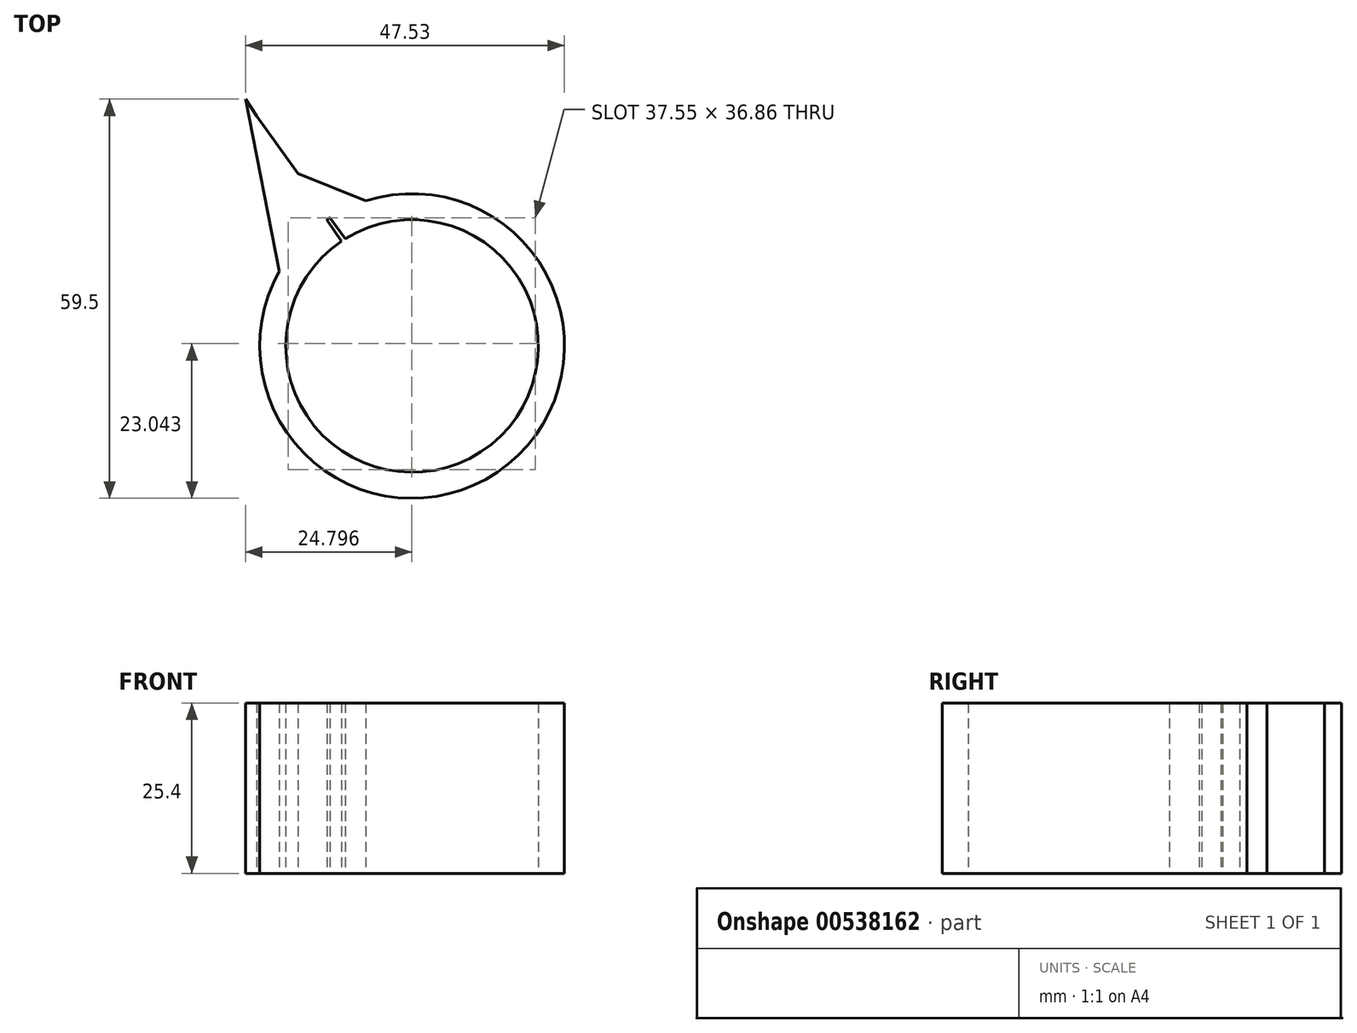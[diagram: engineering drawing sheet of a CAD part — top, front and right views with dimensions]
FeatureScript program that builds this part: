
annotation { "Feature Type Name" : "Feature", "Feature Type Description" : "" }
export const myFeature = defineFeature(function(context is Context, id is Id, definition is map)
    precondition{}
    {
        {
            var Q0;
            Q0=qCreatedBy(makeId("Top.planeOp"),FACE);
            var sketch = newSketch(context, id + "F0", { "sketchPlane" : qUnion([Q0])});
            skCircle(sketch, "E0", {"center": v(0, 0) * mm, "radius": 18.82 * mm});
            skCircle(sketch, "E1", {"center": v(0, 0) * mm, "radius": 22.7 * mm});
            skLineSegment(sketch, "E2", {"start": v(0, 0) * mm, "end": v(-24.83, 36.8) * mm});
            skLineSegment(sketch, "E3", {"start": v(-15.46, -10.74) * mm, "end": v(-24.83, 36.8) * mm});
            skLineSegment(sketch, "E4", {"start": v(11.95, -14.55) * mm, "end": v(-23.14, 34.3) * mm});
            skLineSegment(sketch, "E5", {"start": v(13.06, 13.56) * mm, "end": v(-23.14, 28.21) * mm});
            skLineSegment(sketch, "E6", {"start": v(-9.97, 15.97) * mm, "end": v(-12.07, 2.18) * mm});
            skLineSegment(sketch, "E7", {"start": v(-6.27, -3.3) * mm, "end": v(-1.7, -6.3) * mm});
            skSolve(sketch);
        }
        {
            var Q0;
            Q0 = qSketchRegion(id + "F0", true);
            extrude(context, id + "F1", {"entities" : qUnion([Q0]), "depth" : 25.4 * mm, "offsetDistance" : 25.4 * mm});
        }
    });
